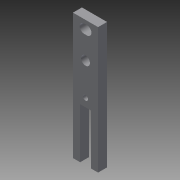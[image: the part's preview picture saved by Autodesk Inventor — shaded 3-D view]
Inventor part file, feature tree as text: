
AUTODESK INVENTOR PART (.ipt)
format: ipt  version: 2013 (Build 170138000, 138)  size: 91,136 bytes
history: native  units: in
note: dims shown in document units (in); Inventor stores cm internally (conversion verified against a paired STEP export)
features: extrude x1, sketch x1
ambient origin geometry x8: Origin, YZ Plane, XZ Plane, XY Plane, X Axis, Y Axis, Z Axis, Center Point
bodies: Solid1 (feature_tree)
feature tree (2):
  extrude  "Extrusion1"  Depth=0.625in
  sketch  "Sketch1"  dims[d1=0.25in d2=0.625in d3=0.5978in d4=0.0412in d7=3.51in d8=0.7in d9=3.51in d10=0.2in d12=1.4in d13=0.3in d15=0.14in d16=0.25in d17=0.0in]
